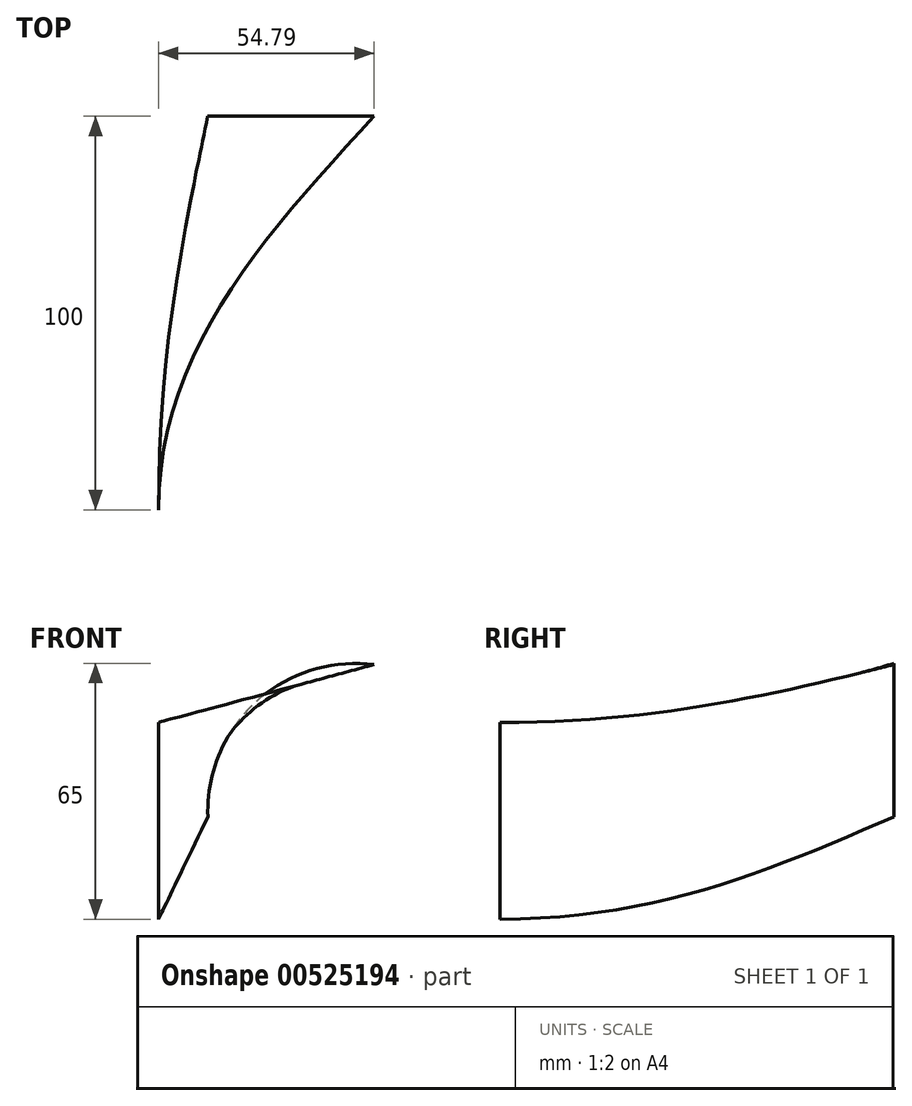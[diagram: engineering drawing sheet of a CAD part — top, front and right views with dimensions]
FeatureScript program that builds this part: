
annotation { "Feature Type Name" : "Feature", "Feature Type Description" : "" }
export const myFeature = defineFeature(function(context is Context, id is Id, definition is map)
    precondition{}
    {
        {
            var Q0;
            Q0=qCreatedBy(makeId("Front.planeOp"),FACE);
            var sketch = newSketch(context, id + "F0", { "sketchPlane" : qUnion([Q0])});
            skArc(sketch, "E0", {"start": v(0, 25) * mm, "mid": v(-25, 0) * mm, "end": v(0, -25) * mm, "construction": true});
            skLineSegment(sketch, "E1", {"start": v(0, 75.58) * mm, "end": v(0, -74.54) * mm, "construction": true});
            skLineSegment(sketch, "E2", {"start": v(-25, 25) * mm, "end": v(-25, -25) * mm});
            skPoint(sketch, "E2.startSnap0", {"position": v(-25, 0) * mm});
            skPoint(sketch, "E2.endSnap0", {"position": v(-25, 0) * mm});
            skSolve(sketch);
        }
        {
            var Q0;
            Q0=qCreatedBy(makeId("Front.planeOp"),FACE);
            cPlane(context, id + "F1", {"entities" : qUnion([Q0]), "cplaneType" : CPlaneType.OFFSET, "offset" : 100 * mm, "oppositeDirection" : true, "width" : 150 * mm, "height" : 150 * mm});
        }
        {
            var Q0;
            Q0=qCreatedBy(id+"F1.planeOp",FACE);
            var sketch = newSketch(context, id + "F2", { "sketchPlane" : qUnion([Q0])});
            skLineSegment(sketch, "E3", {"start": v(0, 75.85) * mm, "end": v(0, -74.37) * mm, "construction": true});
            skLineSegment(sketch, "E4", {"start": v(25, 12.5) * mm, "end": v(25, -60.05) * mm, "construction": true});
            skPoint(sketch, "E5", {"position": v(25, 12.5) * mm});
            skLineSegment(sketch, "E6", {"start": v(25, 12.5) * mm, "end": v(43.82, 64.22) * mm, "construction": true});
            skLineSegment(sketch, "E7", {"start": v(25, 12.5) * mm, "end": v(35.63, 72.81) * mm, "construction": true});
            skArc(sketch, "E8.trimOffspring", {"start": v(29.8, 39.7) * mm, "mid": v(-0.32, 30.17) * mm, "end": v(-12.47, 1.02) * mm});
            skLineSegment(sketch, "E9", {"start": v(-12.47, 1.02) * mm, "end": v(-12.47, -50.06) * mm});
            skSolve(sketch);
        }
        {
            var Q0;
            Q0=sQuery(id+"F0.wireOp",EDGE,"E2");
            var Q1;
            Q1=sQuery(id+"F2.wireOp",EDGE,"E8.trimOffspring");
            var Q2;
            Q2=sQuery(id+"F0.wireOp",VERTEX,"E2.start");
            var Q3;
            Q3=sQuery(id+"F2.wireOp",VERTEX,"E8.trimOffspring.start");
            loft(context, id + "F3", {"bodyType" : ToolBodyType.SURFACE, "startCondition" : LoftEndDerivativeType.NORMAL_TO_PROFILE, "startMagnitude" : 1.2, "wireProfilesArray" : [{ "wireProfileEntities" : qUnion([Q0]) }, { "wireProfileEntities" : qUnion([Q1]) }], "matchConnections" : true, "connections" : [{ "connectionEntities" : qUnion([Q2, Q3]), "connectionEdgeQueries" : qUnion([]), "connectionEdgeParameters" : [] }]});
        }
    });
